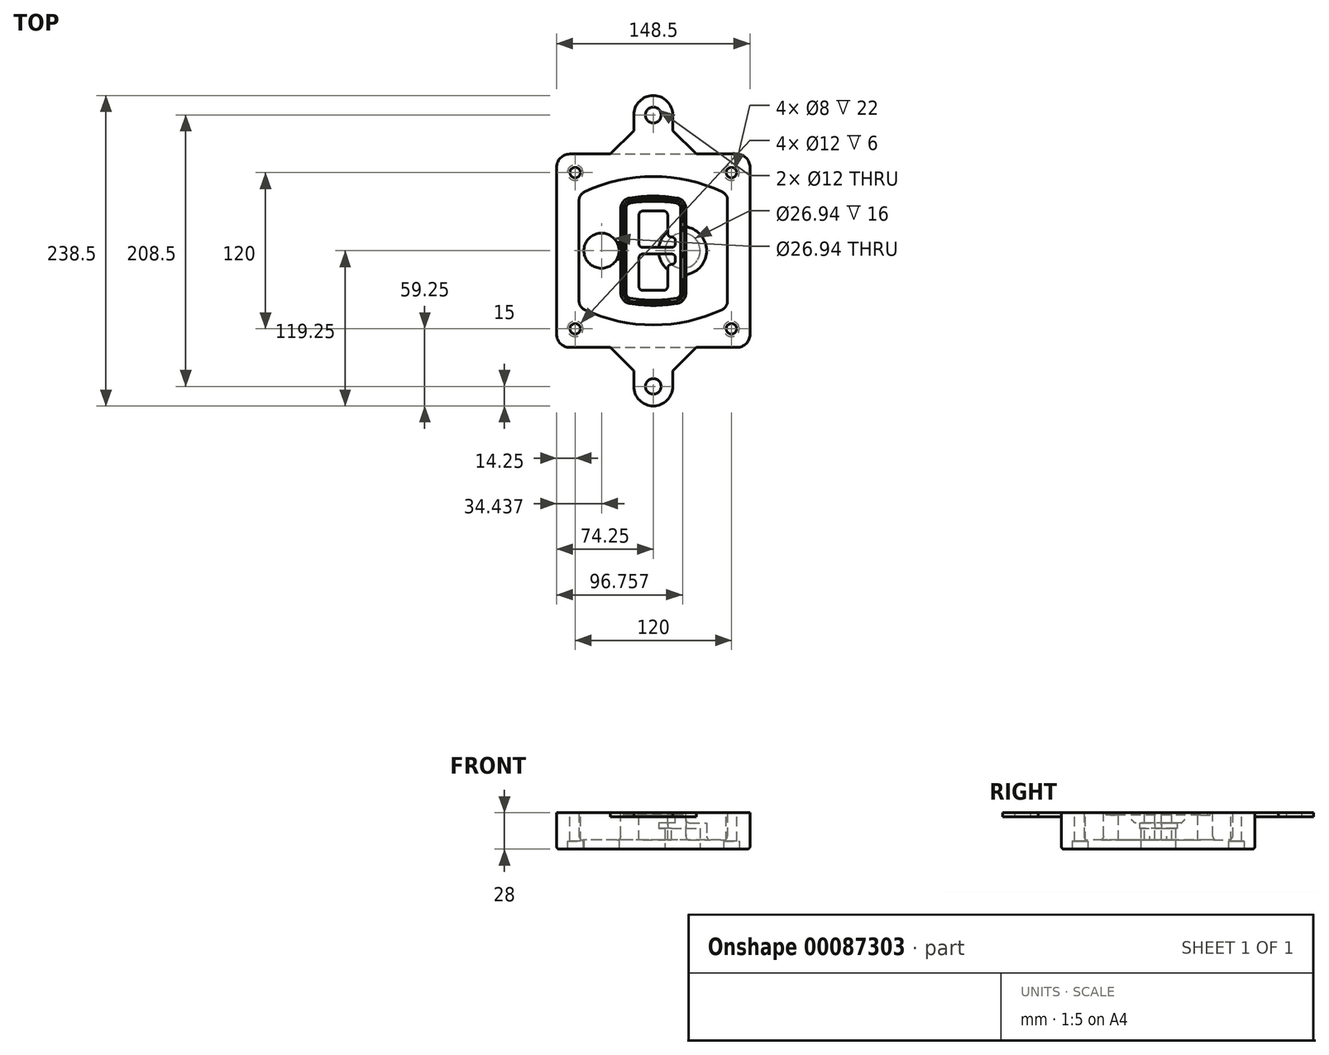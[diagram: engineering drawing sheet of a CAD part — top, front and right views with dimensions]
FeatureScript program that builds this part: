
annotation { "Feature Type Name" : "Feature", "Feature Type Description" : "" }
export const myFeature = defineFeature(function(context is Context, id is Id, definition is map)
    precondition{}
    {
        {
            var Q0;
            Q0=qCreatedBy(makeId("Top.planeOp"),FACE);
            var sketch = newSketch(context, id + "F0", { "sketchPlane" : qUnion([Q0])});
            skPoint(sketch, "E0.rect.middle", {"position": v(0, 0) * mm});
            skLineSegment(sketch, "E1.bottom", {"start": v(-64.25, -74.25) * mm, "end": v(64.25, -74.25) * mm});
            skLineSegment(sketch, "E1.top", {"start": v(-64.25, 74.25) * mm, "end": v(64.25, 74.25) * mm});
            skLineSegment(sketch, "E1.left", {"start": v(-74.25, -64.25) * mm, "end": v(-74.25, 64.25) * mm});
            skLineSegment(sketch, "E1.right", {"start": v(74.25, -64.25) * mm, "end": v(74.25, 64.25) * mm});
            skLineSegment(sketch, "E2", {"start": v(-74.25, 74.25) * mm, "end": v(74.25, -74.25) * mm, "construction": true});
            skLineSegment(sketch, "E3", {"start": v(74.25, 74.25) * mm, "end": v(-74.25, -74.25) * mm, "construction": true});
            skCircle(sketch, "E4", {"center": v(-60, 60) * mm, "radius": 4 * mm});
            skCircle(sketch, "E5", {"center": v(60, 60) * mm, "radius": 4 * mm});
            skCircle(sketch, "E6", {"center": v(60, -60) * mm, "radius": 4 * mm});
            skCircle(sketch, "E7", {"center": v(-60, -60) * mm, "radius": 4 * mm});
            skLineSegment(sketch, "E8", {"start": v(-60, 60) * mm, "end": v(60, 60) * mm, "construction": true});
            skLineSegment(sketch, "E9", {"start": v(60, 60) * mm, "end": v(60, -60) * mm, "construction": true});
            skLineSegment(sketch, "E10", {"start": v(60, -60) * mm, "end": v(-60, -60) * mm, "construction": true});
            skLineSegment(sketch, "E11", {"start": v(-60, -60) * mm, "end": v(-60, 60) * mm, "construction": true});
            skLineSegment(sketch, "E12", {"start": v(-60, 38.83) * mm, "end": v(-60, -38.83) * mm});
            skLineSegment(sketch, "E13", {"start": v(60, 38.83) * mm, "end": v(60, -38.83) * mm});
            skArc(sketch, "E14", {"start": v(54.26, 47.88) * mm, "mid": v(0, 60) * mm, "end": v(-54.26, 47.88) * mm});
            skArc(sketch, "E15", {"start": v(-54.26, -47.88) * mm, "mid": v(0, -60) * mm, "end": v(54.26, -47.88) * mm});
            skLineSegment(sketch, "E16", {"start": v(-60, 0) * mm, "end": v(60, 0) * mm, "construction": true});
            skPoint(sketch, "E17.visualSharp", {"position": v(-60, -45) * mm});
            skArc(sketch, "E17.filletArc", {"start": v(-60, -38.83) * mm, "mid": v(-58.44, -44.2) * mm, "end": v(-54.26, -47.88) * mm});
            skPoint(sketch, "E18.visualSharp", {"position": v(-60, 45) * mm});
            skArc(sketch, "E18.filletArc", {"start": v(-54.26, 47.88) * mm, "mid": v(-58.44, 44.2) * mm, "end": v(-60, 38.83) * mm});
            skPoint(sketch, "E19.visualSharp", {"position": v(60, 45) * mm});
            skArc(sketch, "E19.filletArc", {"start": v(60, 38.83) * mm, "mid": v(58.44, 44.2) * mm, "end": v(54.26, 47.88) * mm});
            skPoint(sketch, "E20.visualSharp", {"position": v(60, -45) * mm});
            skArc(sketch, "E20.filletArc", {"start": v(54.26, -47.88) * mm, "mid": v(58.44, -44.2) * mm, "end": v(60, -38.83) * mm});
            skPoint(sketch, "E21.visualSharp", {"position": v(-74.25, 74.25) * mm});
            skArc(sketch, "E21.filletArc", {"start": v(-64.25, 74.25) * mm, "mid": v(-71.32, 71.32) * mm, "end": v(-74.25, 64.25) * mm});
            skPoint(sketch, "E22.visualSharp", {"position": v(74.25, 74.25) * mm});
            skArc(sketch, "E22.filletArc", {"start": v(74.25, 64.25) * mm, "mid": v(71.32, 71.32) * mm, "end": v(64.25, 74.25) * mm});
            skPoint(sketch, "E23.visualSharp", {"position": v(74.25, -74.25) * mm});
            skArc(sketch, "E23.filletArc", {"start": v(64.25, -74.25) * mm, "mid": v(71.32, -71.32) * mm, "end": v(74.25, -64.25) * mm});
            skPoint(sketch, "E24.visualSharp", {"position": v(-74.25, -74.25) * mm});
            skArc(sketch, "E24.filletArc", {"start": v(-74.25, -64.25) * mm, "mid": v(-71.32, -71.32) * mm, "end": v(-64.25, -74.25) * mm});
            skArc(sketch, "E25.0", {"start": v(57, 38.83) * mm, "mid": v(55.9, 42.58) * mm, "end": v(52.98, 45.17) * mm});
            skLineSegment(sketch, "E25.1", {"start": v(57, 38.83) * mm, "end": v(57, -38.83) * mm});
            skArc(sketch, "E25.2", {"start": v(52.98, -45.17) * mm, "mid": v(55.9, -42.58) * mm, "end": v(57, -38.83) * mm});
            skArc(sketch, "E25.3", {"start": v(-52.98, -45.17) * mm, "mid": v(0, -57) * mm, "end": v(52.98, -45.17) * mm});
            skArc(sketch, "E25.4", {"start": v(-57, -38.83) * mm, "mid": v(-55.9, -42.58) * mm, "end": v(-52.98, -45.17) * mm});
            skArc(sketch, "E25.5", {"start": v(52.98, 45.17) * mm, "mid": v(0, 57) * mm, "end": v(-52.98, 45.17) * mm});
            skLineSegment(sketch, "E25.6", {"start": v(-57, 38.83) * mm, "end": v(-57, -38.83) * mm});
            skArc(sketch, "E25.7", {"start": v(-52.98, 45.17) * mm, "mid": v(-55.9, 42.58) * mm, "end": v(-57, 38.83) * mm});
            skArc(sketch, "E26.0", {"start": v(-55.96, 51.5) * mm, "mid": v(-61.82, 46.33) * mm, "end": v(-64, 38.83) * mm});
            skArc(sketch, "E26.1", {"start": v(55.96, 51.5) * mm, "mid": v(0, 64) * mm, "end": v(-55.96, 51.5) * mm});
            skArc(sketch, "E26.2", {"start": v(64, 38.83) * mm, "mid": v(61.82, 46.33) * mm, "end": v(55.96, 51.5) * mm});
            skLineSegment(sketch, "E26.3", {"start": v(64, 38.83) * mm, "end": v(64, -38.83) * mm});
            skArc(sketch, "E26.4", {"start": v(55.96, -51.5) * mm, "mid": v(61.82, -46.33) * mm, "end": v(64, -38.83) * mm});
            skLineSegment(sketch, "E26.5", {"start": v(-64, 38.83) * mm, "end": v(-64, -38.83) * mm});
            skArc(sketch, "E26.6", {"start": v(-55.96, -51.5) * mm, "mid": v(0, -64) * mm, "end": v(55.96, -51.5) * mm});
            skArc(sketch, "E26.7", {"start": v(-64, -38.83) * mm, "mid": v(-61.82, -46.33) * mm, "end": v(-55.96, -51.5) * mm});
            skSolve(sketch);
        }
        {
            var Q0;
            Q0=makeQuery(id+"F0.imprint","IMPRINT",FACE,{"disambiguationData":[TD([[makeQuery(id+"F0.imprint","IMPRINT",EDGE,{"derivedFrom":sQuery(id+"F0.wireOp",EDGE,"E1.bottom")}),1.0]])]});
            var Q1;
            Q1=makeQuery(id+"F0.imprint","IMPRINT",FACE,{"disambiguationData":[TD([[makeQuery(id+"F0.imprint","IMPRINT",EDGE,{"derivedFrom":sQuery(id+"F0.wireOp",EDGE,"E12")}),1.0]])]});
            var Q2;
            Q2=makeQuery(id+"F0.imprint","IMPRINT",FACE,{"disambiguationData":[TD([[makeQuery(id+"F0.imprint","IMPRINT",EDGE,{"derivedFrom":sQuery(id+"F0.wireOp",EDGE,"E25.0")}),1.0]])]});
            var Q3;
            Q3=makeQuery(id+"F0.imprint","IMPRINT",FACE,{"disambiguationData":[TD([[makeQuery(id+"F0.imprint","IMPRINT",EDGE,{"derivedFrom":sQuery(id+"F0.wireOp",EDGE,"E12")}),-1.0]])]});
            extrude(context, id + "F1", {"entities" : qUnion([Q0, Q1, Q2, Q3]), "oppositeDirection" : true, "depth" : 25 * mm});
        }
        {
            var Q0;
            Q0=makeQuery(id+"F0.imprint","IMPRINT",FACE,{"disambiguationData":[TD([[makeQuery(id+"F0.imprint","IMPRINT",EDGE,{"derivedFrom":sQuery(id+"F0.wireOp",EDGE,"E12")}),1.0]])]});
            extrude(context, id + "F2", {"entities" : qUnion([Q0]), "operationType" : NewBodyOperationType.ADD, "depth" : 3 * mm});
        }
        {
            var Q0;
            Q0=makeQuery(id+"F0.imprint","IMPRINT",FACE,{"disambiguationData":[TD([[makeQuery(id+"F0.imprint","IMPRINT",EDGE,{"derivedFrom":sQuery(id+"F0.wireOp",EDGE,"E25.0")}),1.0]])]});
            extrude(context, id + "F3", {"entities" : qUnion([Q0]), "operationType" : NewBodyOperationType.REMOVE, "oppositeDirection" : true, "depth" : 18 * mm});
        }
        {
            var Q0;
            Q0=makeQuery(id+"F2.opExtrude","CAP_FACE",FACE,{"disambiguationData":[OSD([sQuery(id+"F0.wireOp",EDGE,"E12"),sQuery(id+"F0.wireOp",EDGE,"E13"),sQuery(id+"F0.wireOp",EDGE,"E14"),sQuery(id+"F0.wireOp",EDGE,"E15"),sQuery(id+"F0.wireOp",EDGE,"E17.filletArc"),sQuery(id+"F0.wireOp",EDGE,"E18.filletArc"),sQuery(id+"F0.wireOp",EDGE,"E19.filletArc"),sQuery(id+"F0.wireOp",EDGE,"E20.filletArc"),sQuery(id+"F0.wireOp",EDGE,"E25.0"),sQuery(id+"F0.wireOp",EDGE,"E25.1"),sQuery(id+"F0.wireOp",EDGE,"E25.2"),sQuery(id+"F0.wireOp",EDGE,"E25.3"),sQuery(id+"F0.wireOp",EDGE,"E25.4"),sQuery(id+"F0.wireOp",EDGE,"E25.5"),sQuery(id+"F0.wireOp",EDGE,"E25.6"),sQuery(id+"F0.wireOp",EDGE,"E25.7")])],"isStart":false});
            var sketch = newSketch(context, id + "F4", { "sketchPlane" : qUnion([Q0])});
            skArc(sketch, "E27.0", {"start": v(-18.34, -40.45) * mm, "mid": v(0, -42) * mm, "end": v(18.34, -40.45) * mm});
            skArc(sketch, "E28.0", {"start": v(18.34, 40.45) * mm, "mid": v(0, 42) * mm, "end": v(-18.34, 40.45) * mm});
            skLineSegment(sketch, "E29", {"start": v(-25, 32.57) * mm, "end": v(-25, -32.57) * mm});
            skLineSegment(sketch, "E30", {"start": v(25, 32.57) * mm, "end": v(25, -32.57) * mm});
            skLineSegment(sketch, "E31", {"start": v(-25, 39.1) * mm, "end": v(25, 39.1) * mm, "construction": true});
            skLineSegment(sketch, "E32", {"start": v(-25, -39.1) * mm, "end": v(25, -39.1) * mm, "construction": true});
            skPoint(sketch, "E33.visualSharp", {"position": v(-25, 39.1) * mm});
            skArc(sketch, "E33.filletArc", {"start": v(-18.34, 40.45) * mm, "mid": v(-23.11, 37.73) * mm, "end": v(-25, 32.57) * mm});
            skPoint(sketch, "E34.visualSharp", {"position": v(25, 39.1) * mm});
            skArc(sketch, "E34.filletArc", {"start": v(25, 32.57) * mm, "mid": v(23.11, 37.73) * mm, "end": v(18.34, 40.45) * mm});
            skPoint(sketch, "E35.visualSharp", {"position": v(25, -39.1) * mm});
            skArc(sketch, "E35.filletArc", {"start": v(18.34, -40.45) * mm, "mid": v(23.11, -37.73) * mm, "end": v(25, -32.57) * mm});
            skPoint(sketch, "E36.visualSharp", {"position": v(-25, -39.1) * mm});
            skArc(sketch, "E36.filletArc", {"start": v(-25, -32.57) * mm, "mid": v(-23.11, -37.73) * mm, "end": v(-18.34, -40.45) * mm});
            skArc(sketch, "E37.0", {"start": v(52.98, 45.17) * mm, "mid": v(0, 57) * mm, "end": v(-52.98, 45.17) * mm});
            skArc(sketch, "E37.1", {"start": v(-52.98, 45.17) * mm, "mid": v(-55.9, 42.58) * mm, "end": v(-57, 38.83) * mm});
            skLineSegment(sketch, "E37.2", {"start": v(-57, 38.83) * mm, "end": v(-57, -38.83) * mm});
            skArc(sketch, "E37.3", {"start": v(-57, -38.83) * mm, "mid": v(-55.9, -42.58) * mm, "end": v(-52.98, -45.17) * mm});
            skArc(sketch, "E37.4", {"start": v(-52.98, -45.17) * mm, "mid": v(0, -57) * mm, "end": v(52.98, -45.17) * mm});
            skArc(sketch, "E37.5", {"start": v(52.98, -45.17) * mm, "mid": v(55.9, -42.58) * mm, "end": v(57, -38.83) * mm});
            skLineSegment(sketch, "E37.6", {"start": v(57, 38.83) * mm, "end": v(57, -38.83) * mm});
            skArc(sketch, "E37.7", {"start": v(57, 38.83) * mm, "mid": v(55.9, 42.58) * mm, "end": v(52.98, 45.17) * mm});
            skLineSegment(sketch, "E38.0", {"start": v(23, 32.57) * mm, "end": v(23, -32.57) * mm});
            skArc(sketch, "E38.1", {"start": v(18, -38.48) * mm, "mid": v(21.58, -36.44) * mm, "end": v(23, -32.57) * mm});
            skArc(sketch, "E38.2", {"start": v(-18, -38.48) * mm, "mid": v(0, -40) * mm, "end": v(18, -38.48) * mm});
            skArc(sketch, "E38.3", {"start": v(-23, -32.57) * mm, "mid": v(-21.58, -36.44) * mm, "end": v(-18, -38.48) * mm});
            skLineSegment(sketch, "E38.4", {"start": v(-23, 32.57) * mm, "end": v(-23, -32.57) * mm});
            skArc(sketch, "E38.5", {"start": v(23, 32.57) * mm, "mid": v(21.58, 36.44) * mm, "end": v(18, 38.48) * mm});
            skArc(sketch, "E38.6", {"start": v(-18, 38.48) * mm, "mid": v(-21.58, 36.44) * mm, "end": v(-23, 32.57) * mm});
            skArc(sketch, "E38.7", {"start": v(18, 38.48) * mm, "mid": v(0, 40) * mm, "end": v(-18, 38.48) * mm});
            skArc(sketch, "E39.0", {"start": v(21, 32.57) * mm, "mid": v(20.06, 35.15) * mm, "end": v(17.67, 36.5) * mm});
            skLineSegment(sketch, "E39.1", {"start": v(21, 32.57) * mm, "end": v(21, -32.57) * mm});
            skArc(sketch, "E39.2", {"start": v(17.67, -36.5) * mm, "mid": v(20.06, -35.15) * mm, "end": v(21, -32.57) * mm});
            skArc(sketch, "E39.3", {"start": v(-17.67, -36.5) * mm, "mid": v(0, -38) * mm, "end": v(17.67, -36.5) * mm});
            skArc(sketch, "E39.4", {"start": v(-21, -32.57) * mm, "mid": v(-20.06, -35.15) * mm, "end": v(-17.67, -36.5) * mm});
            skArc(sketch, "E39.5", {"start": v(17.67, 36.5) * mm, "mid": v(0, 38) * mm, "end": v(-17.67, 36.5) * mm});
            skLineSegment(sketch, "E39.6", {"start": v(-21, 32.57) * mm, "end": v(-21, -32.57) * mm});
            skArc(sketch, "E39.7", {"start": v(-17.67, 36.5) * mm, "mid": v(-20.06, 35.15) * mm, "end": v(-21, 32.57) * mm});
            skLineSegment(sketch, "E40", {"start": v(-25, 0) * mm, "end": v(25, 0) * mm, "construction": true});
            skLineSegment(sketch, "E41", {"start": v(-11, 5.5) * mm, "end": v(-11, 27.5) * mm});
            skLineSegment(sketch, "E42", {"start": v(-8, 30.5) * mm, "end": v(8, 30.5) * mm});
            skLineSegment(sketch, "E43", {"start": v(11, 27.5) * mm, "end": v(11, 13.5) * mm});
            skLineSegment(sketch, "E44", {"start": v(14, 10.5) * mm, "end": v(14, 10.5) * mm});
            skLineSegment(sketch, "E45", {"start": v(17, 7.5) * mm, "end": v(17, 5.5) * mm});
            skLineSegment(sketch, "E46", {"start": v(14, 2.5) * mm, "end": v(-8, 2.5) * mm});
            skPoint(sketch, "E47.visualSharp", {"position": v(-11, 30.5) * mm});
            skArc(sketch, "E47.filletArc", {"start": v(-8, 30.5) * mm, "mid": v(-10.12, 29.62) * mm, "end": v(-11, 27.5) * mm});
            skPoint(sketch, "E48.visualSharp", {"position": v(11, 30.5) * mm});
            skArc(sketch, "E48.filletArc", {"start": v(11, 27.5) * mm, "mid": v(10.12, 29.62) * mm, "end": v(8, 30.5) * mm});
            skPoint(sketch, "E49.visualSharp", {"position": v(11, 10.5) * mm});
            skArc(sketch, "E49.filletArc", {"start": v(11, 13.5) * mm, "mid": v(11.88, 11.38) * mm, "end": v(14, 10.5) * mm});
            skPoint(sketch, "E50.visualSharp", {"position": v(17, 10.5) * mm});
            skArc(sketch, "E50.filletArc", {"start": v(17, 7.5) * mm, "mid": v(16.12, 9.62) * mm, "end": v(14, 10.5) * mm});
            skPoint(sketch, "E51.visualSharp", {"position": v(17, 2.5) * mm});
            skArc(sketch, "E51.filletArc", {"start": v(14, 2.5) * mm, "mid": v(16.12, 3.38) * mm, "end": v(17, 5.5) * mm});
            skPoint(sketch, "E52.visualSharp", {"position": v(-11, 2.5) * mm});
            skArc(sketch, "E52.filletArc", {"start": v(-11, 5.5) * mm, "mid": v(-10.12, 3.38) * mm, "end": v(-8, 2.5) * mm});
            skLineSegment(sketch, "E53.0.MirrorCS", {"start": v(14, -2.5) * mm, "end": v(-8, -2.5) * mm});
            skArc(sketch, "E54.0.MirrorCS", {"start": v(-11, -5.5) * mm, "mid": v(-10.12, -3.38) * mm, "end": v(-8, -2.5) * mm});
            skLineSegment(sketch, "E55.0.MirrorCS", {"start": v(-11, -5.5) * mm, "end": v(-11, -27.5) * mm});
            skArc(sketch, "E56.0.MirrorCS", {"start": v(-8, -30.5) * mm, "mid": v(-10.12, -29.62) * mm, "end": v(-11, -27.5) * mm});
            skLineSegment(sketch, "E57.0.MirrorCS", {"start": v(-8, -30.5) * mm, "end": v(8, -30.5) * mm});
            skArc(sketch, "E58.0.MirrorCS", {"start": v(11, -27.5) * mm, "mid": v(10.12, -29.62) * mm, "end": v(8, -30.5) * mm});
            skLineSegment(sketch, "E59.0.MirrorCS", {"start": v(11, -27.5) * mm, "end": v(11, -13.5) * mm});
            skArc(sketch, "E60.0.MirrorCS", {"start": v(11, -13.5) * mm, "mid": v(11.88, -11.38) * mm, "end": v(14, -10.5) * mm});
            skArc(sketch, "E61.0.MirrorCS", {"start": v(17, -7.5) * mm, "mid": v(16.12, -9.62) * mm, "end": v(14, -10.5) * mm});
            skLineSegment(sketch, "E62.0.MirrorCS", {"start": v(17, -7.5) * mm, "end": v(17, -5.5) * mm});
            skArc(sketch, "E63.0.MirrorCS", {"start": v(14, -2.5) * mm, "mid": v(16.12, -3.38) * mm, "end": v(17, -5.5) * mm});
            skSolve(sketch);
        }
        {
            var Q0;
            Q0=makeQuery(id+"F4.imprint","IMPRINT",FACE,{"disambiguationData":[TD([[makeQuery(id+"F4.imprint","IMPRINT",EDGE,{"derivedFrom":sQuery(id+"F4.wireOp",EDGE,"E27.0")}),1.0]])]});
            var Q1;
            Q1=makeQuery(id+"F4.imprint","IMPRINT",FACE,{"disambiguationData":[TD([[makeQuery(id+"F4.imprint","IMPRINT",EDGE,{"derivedFrom":sQuery(id+"F4.wireOp",EDGE,"E38.0")}),-1.0]])]});
            var Q2;
            Q2=makeQuery(id+"F4.imprint","IMPRINT",FACE,{"disambiguationData":[TD([[makeQuery(id+"F4.imprint","IMPRINT",EDGE,{"derivedFrom":sQuery(id+"F4.wireOp",EDGE,"E39.0")}),1.0]])]});
            extrude(context, id + "F5", {"entities" : qUnion([Q0, Q1, Q2]), "operationType" : NewBodyOperationType.ADD, "endBound" : BoundingType.UP_TO_NEXT, "oppositeDirection" : true, "depth" : 25 * mm});
        }
        {
            var Q0;
            Q0=makeQuery(id+"F4.imprint","IMPRINT",FACE,{"disambiguationData":[TD([[makeQuery(id+"F4.imprint","IMPRINT",EDGE,{"derivedFrom":sQuery(id+"F4.wireOp",EDGE,"E38.0")}),-1.0]])]});
            extrude(context, id + "F6", {"entities" : qUnion([Q0]), "operationType" : NewBodyOperationType.REMOVE, "oppositeDirection" : true, "depth" : 2 * mm});
        }
        {
            var Q0;
            Q0=makeQuery(id+"F1.opExtrude","CAP_FACE",FACE,{"disambiguationData":[OSD([sQuery(id+"F0.wireOp",EDGE,"E1.bottom"),sQuery(id+"F0.wireOp",EDGE,"E1.top"),sQuery(id+"F0.wireOp",EDGE,"E1.left"),sQuery(id+"F0.wireOp",EDGE,"E1.right"),sQuery(id+"F0.wireOp",EDGE,"E4"),sQuery(id+"F0.wireOp",EDGE,"E5"),sQuery(id+"F0.wireOp",EDGE,"E6"),sQuery(id+"F0.wireOp",EDGE,"E7"),sQuery(id+"F0.wireOp",EDGE,"E21.filletArc"),sQuery(id+"F0.wireOp",EDGE,"E22.filletArc"),sQuery(id+"F0.wireOp",EDGE,"E23.filletArc"),sQuery(id+"F0.wireOp",EDGE,"E24.filletArc")])],"isStart":false});
            var sketch = newSketch(context, id + "F7", { "sketchPlane" : qUnion([Q0])});
            skCircle(sketch, "E64", {"center": v(22.5, 0) * mm, "radius": 13.47 * mm});
            skCircle(sketch, "E65", {"center": v(-39.81, 0) * mm, "radius": 13.47 * mm});
            skLineSegment(sketch, "E66", {"start": v(74.25, 0) * mm, "end": v(-74.25, 0) * mm});
            skCircle(sketch, "E67", {"center": v(22.5, 0) * mm, "radius": 18.47 * mm});
            skCircle(sketch, "E68", {"center": v(60, -60) * mm, "radius": 6 * mm});
            skCircle(sketch, "E69", {"center": v(-60, -60) * mm, "radius": 6 * mm});
            skCircle(sketch, "E70", {"center": v(-60, 60) * mm, "radius": 6 * mm});
            skCircle(sketch, "E71", {"center": v(60, 60) * mm, "radius": 6 * mm});
            skSolve(sketch);
        }
        {
            var Q0;
            {var subQ1=sQuery(id+"F7.wireOp",EDGE,"E66");var subQ4=sQuery(id+"F7.wireOp",EDGE,"E64");var subQ6=makeQuery(id+"F7.imprint","INTERSECT",VERTEX,{"disambiguationData":[OD(0.0)],"derivedFrom":[subQ4,subQ1]});Q0=makeQuery(id+"F7.imprint","IMPRINT",FACE,{"disambiguationData":[TD([[makeQuery(id+"F7.imprint","IMPRINT",EDGE,{"disambiguationData":[TD([[subQ6,-1.0]])],"derivedFrom":subQ4}),-1.0]])]});}
            var Q1;
            {var subQ0=sQuery(id+"F7.wireOp",EDGE,"E66");var subQ1=sQuery(id+"F7.wireOp",EDGE,"E64");var subQ3=makeQuery(id+"F7.imprint","INTERSECT",VERTEX,{"disambiguationData":[OD(0.0)],"derivedFrom":[subQ1,subQ0]});Q1=makeQuery(id+"F7.imprint","IMPRINT",FACE,{"disambiguationData":[TD([[makeQuery(id+"F7.imprint","IMPRINT",EDGE,{"disambiguationData":[TD([[subQ3,-1.0]])],"derivedFrom":subQ1}),1.0]])]});}
            var Q2;
            {var subQ0=sQuery(id+"F7.wireOp",EDGE,"E66");var subQ1=sQuery(id+"F7.wireOp",EDGE,"E64");var subQ3=makeQuery(id+"F7.imprint","INTERSECT",VERTEX,{"disambiguationData":[OD(0.0)],"derivedFrom":[subQ1,subQ0]});Q2=makeQuery(id+"F7.imprint","IMPRINT",FACE,{"disambiguationData":[TD([[makeQuery(id+"F7.imprint","IMPRINT",EDGE,{"disambiguationData":[TD([[subQ3,1.0]])],"derivedFrom":subQ1}),1.0]])]});}
            var Q3;
            {var subQ1=sQuery(id+"F7.wireOp",EDGE,"E66");var subQ4=sQuery(id+"F7.wireOp",EDGE,"E64");var subQ6=makeQuery(id+"F7.imprint","INTERSECT",VERTEX,{"disambiguationData":[OD(0.0)],"derivedFrom":[subQ4,subQ1]});Q3=makeQuery(id+"F7.imprint","IMPRINT",FACE,{"disambiguationData":[TD([[makeQuery(id+"F7.imprint","IMPRINT",EDGE,{"disambiguationData":[TD([[subQ6,1.0]])],"derivedFrom":subQ4}),-1.0]])]});}
            extrude(context, id + "F8", {"entities" : qUnion([Q0, Q1, Q2, Q3]), "operationType" : NewBodyOperationType.ADD, "oppositeDirection" : true, "depth" : 20 * mm});
        }
        {
            var Q0;
            {var subQ0=sQuery(id+"F7.wireOp",EDGE,"E66");var subQ1=sQuery(id+"F7.wireOp",EDGE,"E64");var subQ3=makeQuery(id+"F7.imprint","INTERSECT",VERTEX,{"disambiguationData":[OD(0.0)],"derivedFrom":[subQ1,subQ0]});Q0=makeQuery(id+"F7.imprint","IMPRINT",FACE,{"disambiguationData":[TD([[makeQuery(id+"F7.imprint","IMPRINT",EDGE,{"disambiguationData":[TD([[subQ3,-1.0]])],"derivedFrom":subQ1}),1.0]])]});}
            var Q1;
            {var subQ0=sQuery(id+"F7.wireOp",EDGE,"E66");var subQ1=sQuery(id+"F7.wireOp",EDGE,"E64");var subQ3=makeQuery(id+"F7.imprint","INTERSECT",VERTEX,{"disambiguationData":[OD(0.0)],"derivedFrom":[subQ1,subQ0]});Q1=makeQuery(id+"F7.imprint","IMPRINT",FACE,{"disambiguationData":[TD([[makeQuery(id+"F7.imprint","IMPRINT",EDGE,{"disambiguationData":[TD([[subQ3,1.0]])],"derivedFrom":subQ1}),1.0]])]});}
            extrude(context, id + "F9", {"entities" : qUnion([Q0, Q1]), "operationType" : NewBodyOperationType.REMOVE, "oppositeDirection" : true, "depth" : 16 * mm});
        }
        {
            var Q0;
            {var subQ0=sQuery(id+"F7.wireOp",EDGE,"E66");var subQ1=sQuery(id+"F7.wireOp",EDGE,"E65");var subQ3=makeQuery(id+"F7.imprint","INTERSECT",VERTEX,{"disambiguationData":[OD(0.0)],"derivedFrom":[subQ1,subQ0]});Q0=makeQuery(id+"F7.imprint","IMPRINT",FACE,{"disambiguationData":[TD([[makeQuery(id+"F7.imprint","IMPRINT",EDGE,{"disambiguationData":[TD([[subQ3,-1.0]])],"derivedFrom":subQ1}),1.0]])]});}
            var Q1;
            {var subQ0=sQuery(id+"F7.wireOp",EDGE,"E66");var subQ1=sQuery(id+"F7.wireOp",EDGE,"E65");var subQ3=makeQuery(id+"F7.imprint","INTERSECT",VERTEX,{"disambiguationData":[OD(0.0)],"derivedFrom":[subQ1,subQ0]});Q1=makeQuery(id+"F7.imprint","IMPRINT",FACE,{"disambiguationData":[TD([[makeQuery(id+"F7.imprint","IMPRINT",EDGE,{"disambiguationData":[TD([[subQ3,1.0]])],"derivedFrom":subQ1}),1.0]])]});}
            extrude(context, id + "F10", {"entities" : qUnion([Q0, Q1]), "operationType" : NewBodyOperationType.REMOVE, "oppositeDirection" : true, "depth" : 25 * mm});
        }
        {
            var Q0;
            Q0=makeQuery(id+"F7.imprint","IMPRINT",FACE,{"disambiguationData":[TD([[makeQuery(id+"F7.imprint","IMPRINT",EDGE,{"derivedFrom":sQuery(id+"F7.wireOp",EDGE,"E68")}),1.0]])]});
            var Q1;
            Q1=makeQuery(id+"F7.imprint","IMPRINT",FACE,{"disambiguationData":[TD([[makeQuery(id+"F7.imprint","IMPRINT",EDGE,{"derivedFrom":makeQuery(id+"F1.opExtrude","CAP_EDGE",EDGE,{"disambiguationData":[OSD([sQuery(id+"F0.wireOp",EDGE,"E5")])],"isStart":false})}),-1.0]])]});
            var Q2;
            Q2=makeQuery(id+"F7.imprint","IMPRINT",FACE,{"disambiguationData":[TD([[makeQuery(id+"F7.imprint","IMPRINT",EDGE,{"derivedFrom":sQuery(id+"F7.wireOp",EDGE,"E69")}),1.0]])]});
            var Q3;
            Q3=makeQuery(id+"F7.imprint","IMPRINT",FACE,{"disambiguationData":[TD([[makeQuery(id+"F7.imprint","IMPRINT",EDGE,{"derivedFrom":makeQuery(id+"F1.opExtrude","CAP_EDGE",EDGE,{"disambiguationData":[OSD([sQuery(id+"F0.wireOp",EDGE,"E4")])],"isStart":false})}),-1.0]])]});
            var Q4;
            Q4=makeQuery(id+"F7.imprint","IMPRINT",FACE,{"disambiguationData":[TD([[makeQuery(id+"F7.imprint","IMPRINT",EDGE,{"derivedFrom":sQuery(id+"F7.wireOp",EDGE,"E70")}),1.0]])]});
            var Q5;
            Q5=makeQuery(id+"F7.imprint","IMPRINT",FACE,{"disambiguationData":[TD([[makeQuery(id+"F7.imprint","IMPRINT",EDGE,{"derivedFrom":makeQuery(id+"F1.opExtrude","CAP_EDGE",EDGE,{"disambiguationData":[OSD([sQuery(id+"F0.wireOp",EDGE,"E7")])],"isStart":false})}),-1.0]])]});
            var Q6;
            Q6=makeQuery(id+"F7.imprint","IMPRINT",FACE,{"disambiguationData":[TD([[makeQuery(id+"F7.imprint","IMPRINT",EDGE,{"derivedFrom":sQuery(id+"F7.wireOp",EDGE,"E71")}),1.0]])]});
            var Q7;
            Q7=makeQuery(id+"F7.imprint","IMPRINT",FACE,{"disambiguationData":[TD([[makeQuery(id+"F7.imprint","IMPRINT",EDGE,{"derivedFrom":makeQuery(id+"F1.opExtrude","CAP_EDGE",EDGE,{"disambiguationData":[OSD([sQuery(id+"F0.wireOp",EDGE,"E6")])],"isStart":false})}),-1.0]])]});
            extrude(context, id + "F11", {"entities" : qUnion([Q0, Q1, Q2, Q3, Q4, Q5, Q6, Q7]), "operationType" : NewBodyOperationType.REMOVE, "oppositeDirection" : true, "depth" : 6 * mm});
        }
        {
            var Q0;
            Q0=makeQuery(id+"F9.boolean.opBoolean","COPY",FACE,{"derivedFrom":makeQuery(id+"F9.opExtrude","CAP_FACE",FACE,{"disambiguationData":[OSD([sQuery(id+"F7.wireOp",EDGE,"E64")])],"isStart":false})});
            var sketch = newSketch(context, id + "F12", { "sketchPlane" : qUnion([Q0])});
            skArc(sketch, "E72.0", {"start": v(11, 14.45) * mm, "mid": v(6.45, 9.13) * mm, "end": v(4.2, 2.5) * mm});
            skArc(sketch, "E72.1", {"start": v(4.2, -2.5) * mm, "mid": v(6.45, -9.13) * mm, "end": v(11, -14.45) * mm});
            skLineSegment(sketch, "E73", {"start": v(4.2, -2.5) * mm, "end": v(14, -2.5) * mm});
            skLineSegment(sketch, "E74.0", {"start": v(14, 2.5) * mm, "end": v(4.2, 2.5) * mm});
            skArc(sketch, "E74.1", {"start": v(14, 2.5) * mm, "mid": v(16.12, 3.38) * mm, "end": v(17, 5.5) * mm});
            skLineSegment(sketch, "E74.2", {"start": v(17, 7.5) * mm, "end": v(17, 5.5) * mm});
            skArc(sketch, "E74.3", {"start": v(17, 7.5) * mm, "mid": v(16.12, 9.62) * mm, "end": v(14, 10.5) * mm});
            skArc(sketch, "E74.4", {"start": v(11, 13.5) * mm, "mid": v(11.88, 11.38) * mm, "end": v(14, 10.5) * mm});
            skLineSegment(sketch, "E74.5", {"start": v(11, 14.45) * mm, "end": v(11, 13.5) * mm});
            skLineSegment(sketch, "E74.7", {"start": v(14, -2.5) * mm, "end": v(4.2, -2.5) * mm});
            skArc(sketch, "E74.8", {"start": v(14, -2.5) * mm, "mid": v(16.12, -3.38) * mm, "end": v(17, -5.5) * mm});
            skLineSegment(sketch, "E74.9", {"start": v(17, -7.5) * mm, "end": v(17, -5.5) * mm});
            skArc(sketch, "E74.10", {"start": v(17, -7.5) * mm, "mid": v(16.12, -9.62) * mm, "end": v(14, -10.5) * mm});
            skArc(sketch, "E74.11", {"start": v(11, -13.5) * mm, "mid": v(11.88, -11.38) * mm, "end": v(14, -10.5) * mm});
            skLineSegment(sketch, "E74.12", {"start": v(11, -14.45) * mm, "end": v(11, -13.5) * mm});
            skPoint(sketch, "E75.orphan", {"position": v(11, -27.5) * mm});
            skPoint(sketch, "E76.orphan", {"position": v(-8, -2.5) * mm});
            skPoint(sketch, "E77.orphan", {"position": v(-8, 2.5) * mm});
            skPoint(sketch, "E78.orphan", {"position": v(11, 27.5) * mm});
            skSolve(sketch);
        }
        {
            var Q0;
            {var subQ7=sQuery(id+"F12.wireOp",EDGE,"E72.0");var subQ14=sQuery(id+"F12.wireOp",EDGE,"E72.1");var subQ16=sQuery(id+"F12.wireOp",EDGE,"E74.1");var subQ18=sQuery(id+"F12.wireOp",EDGE,"E74.8");Q0=qUnion([makeQuery(id+"F12.imprint","IMPRINT",FACE,{"disambiguationData":[TD([[makeQuery(id+"F12.imprint","IMPRINT",EDGE,{"derivedFrom":subQ7}),1.0]])]}),makeQuery(id+"F12.imprint","IMPRINT",FACE,{"disambiguationData":[TD([[makeQuery(id+"F12.imprint","IMPRINT",EDGE,{"derivedFrom":subQ14}),1.0]])]}),makeQuery(id+"F12.imprint","IMPRINT",FACE,{"disambiguationData":[TD([[makeQuery(id+"F12.imprint","IMPRINT",EDGE,{"derivedFrom":subQ16}),1.0]])]}),makeQuery(id+"F12.imprint","IMPRINT",FACE,{"disambiguationData":[TD([[makeQuery(id+"F12.imprint","IMPRINT",EDGE,{"derivedFrom":subQ18}),-1.0]])]})]);}
            var Q1;
            Q1=makeQuery(id+"F5.boolean.opBoolean","SPLIT",FACE,{"disambiguationData":[TD([makeQuery(id+"F5.opExtrude","SWEPT_FACE",FACE,{"disambiguationData":[OSD([sQuery(id+"F4.wireOp",EDGE,"E41")])]})])],"derivedFrom":makeQuery(id+"F3.boolean.opBoolean","COPY",FACE,{"derivedFrom":makeQuery(id+"F3.opExtrude","CAP_FACE",FACE,{"disambiguationData":[OSD([sQuery(id+"F0.wireOp",EDGE,"E25.0"),sQuery(id+"F0.wireOp",EDGE,"E25.1"),sQuery(id+"F0.wireOp",EDGE,"E25.2"),sQuery(id+"F0.wireOp",EDGE,"E25.3"),sQuery(id+"F0.wireOp",EDGE,"E25.4"),sQuery(id+"F0.wireOp",EDGE,"E25.5"),sQuery(id+"F0.wireOp",EDGE,"E25.6"),sQuery(id+"F0.wireOp",EDGE,"E25.7")])],"isStart":false})})});
            extrude(context, id + "F13", {"entities" : qUnion([Q0]), "operationType" : NewBodyOperationType.REMOVE, "endBound" : BoundingType.UP_TO_SURFACE, "endBoundEntityFace" : qUnion([Q1]), "depth" : 25 * mm});
        }
        {
            var Q0;
            Q0=makeQuery(id+"F3.boolean.opBoolean","COPY",EDGE,{"derivedFrom":makeQuery(id+"F3.opExtrude","CAP_EDGE",EDGE,{"disambiguationData":[OSD([sQuery(id+"F0.wireOp",EDGE,"E25.6")])],"isStart":false})});
            var Q1;
            Q1=makeQuery(id+"F8.boolean.opBoolean","INTERSECT",EDGE,{"derivedFrom":[makeQuery(id+"F5.opExtrude","SWEPT_FACE",FACE,{"disambiguationData":[OSD([sQuery(id+"F4.wireOp",EDGE,"E30")])]}),makeQuery(id+"F8.opExtrude","CAP_FACE",FACE,{"disambiguationData":[OSD([sQuery(id+"F7.wireOp",EDGE,"E67")])],"isStart":false})]});
            var Q2;
            Q2=makeQuery(id+"F8.boolean.opBoolean","INTERSECT",EDGE,{"disambiguationData":[OD(1.0)],"derivedFrom":[makeQuery(id+"F5.opExtrude","SWEPT_FACE",FACE,{"disambiguationData":[OSD([sQuery(id+"F4.wireOp",EDGE,"E30")])]}),makeQuery(id+"F8.opExtrude","SWEPT_FACE",FACE,{"disambiguationData":[OSD([sQuery(id+"F7.wireOp",EDGE,"E67")])]})]});
            var Q3;
            {var subQ0=sQuery(id+"F4.wireOp",EDGE,"E30");Q3=makeQuery(id+"F8.boolean.opBoolean","SPLIT",EDGE,{"disambiguationData":[TD([makeQuery(id+"F5.opExtrude","SWEPT_FACE",FACE,{"disambiguationData":[OSD([sQuery(id+"F4.wireOp",EDGE,"E35.filletArc")])]})])],"derivedFrom":makeQuery(id+"F5.opExtrude","CAP_EDGE",EDGE,{"disambiguationData":[OSD([subQ0])],"isStart":false})});}
            var Q4;
            {var subQ0=sQuery(id+"F0.wireOp",EDGE,"E25.7");var subQ1=sQuery(id+"F0.wireOp",EDGE,"E25.1");var subQ2=sQuery(id+"F0.wireOp",EDGE,"E25.6");var subQ3=sQuery(id+"F0.wireOp",EDGE,"E25.5");var subQ4=sQuery(id+"F0.wireOp",EDGE,"E25.4");var subQ5=sQuery(id+"F0.wireOp",EDGE,"E25.0");var subQ6=sQuery(id+"F0.wireOp",EDGE,"E25.2");var subQ7=sQuery(id+"F0.wireOp",EDGE,"E25.3");Q4=makeQuery(id+"F8.boolean.opBoolean","INTERSECT",EDGE,{"derivedFrom":[makeQuery(id+"F5.boolean.opBoolean","SPLIT",FACE,{"disambiguationData":[TD([makeQuery(id+"F2.opExtrude","SWEPT_FACE",FACE,{"disambiguationData":[OSD([subQ5])]})])],"derivedFrom":makeQuery(id+"F3.boolean.opBoolean","COPY",FACE,{"derivedFrom":makeQuery(id+"F3.opExtrude","CAP_FACE",FACE,{"disambiguationData":[OSD([subQ5,subQ1,subQ6,subQ7,subQ4,subQ3,subQ2,subQ0])],"isStart":false})})}),makeQuery(id+"F8.opExtrude","SWEPT_FACE",FACE,{"disambiguationData":[OSD([sQuery(id+"F7.wireOp",EDGE,"E67")])]})]});}
            var Q5;
            Q5=makeQuery(id+"F8.boolean.opBoolean","INTERSECT",EDGE,{"disambiguationData":[OD(0.0)],"derivedFrom":[makeQuery(id+"F5.opExtrude","SWEPT_FACE",FACE,{"disambiguationData":[OSD([sQuery(id+"F4.wireOp",EDGE,"E30")])]}),makeQuery(id+"F8.opExtrude","SWEPT_FACE",FACE,{"disambiguationData":[OSD([sQuery(id+"F7.wireOp",EDGE,"E67")])]})]});
            fillet(context, id + "F14", {"entities" : qUnion([Q0, Q1, Q2, Q3, Q4, Q5]), "radius" : 3 * mm, "tangentPropagation" : true, "allowEdgeOverflow" : false});
        }
        {
            var Q0;
            Q0=makeQuery(id+"F1.opExtrude","CAP_EDGE",EDGE,{"disambiguationData":[OSD([sQuery(id+"F0.wireOp",EDGE,"E1.bottom")])],"isStart":false});
            fillet(context, id + "F15", {"entities" : qUnion([Q0]), "radius" : 2 * mm, "tangentPropagation" : true, "allowEdgeOverflow" : false});
        }
        {
            var Q0;
            Q0=qCreatedBy(makeId("Top.planeOp"),FACE);
            var sketch = newSketch(context, id + "F16", { "sketchPlane" : qUnion([Q0])});
            skLineSegment(sketch, "E79.0", {"start": v(-64.25, 74.25) * mm, "end": v(64.25, 74.25) * mm});
            skLineSegment(sketch, "E80.0", {"start": v(-64.25, -74.25) * mm, "end": v(64.25, -74.25) * mm});
            skLineSegment(sketch, "E81", {"start": v(0, 74.25) * mm, "end": v(0, 104.25) * mm, "construction": true});
            skCircle(sketch, "E82", {"center": v(0, 104.25) * mm, "radius": 6 * mm});
            skLineSegment(sketch, "E83", {"start": v(15, 104.25) * mm, "end": v(15, 92.25) * mm});
            skLineSegment(sketch, "E84", {"start": v(-15, 104.25) * mm, "end": v(-15, 92.25) * mm});
            skLineSegment(sketch, "E85", {"start": v(-15, 92.25) * mm, "end": v(-33, 74.25) * mm});
            skLineSegment(sketch, "E86", {"start": v(15, 92.25) * mm, "end": v(33, 74.25) * mm});
            skArc(sketch, "E87", {"start": v(15, 104.25) * mm, "mid": v(0, 119.25) * mm, "end": v(-15, 104.25) * mm});
            skLineSegment(sketch, "E88", {"start": v(0, 0) * mm, "end": v(107.6, 0) * mm, "construction": true});
            skLineSegment(sketch, "E89.MirrorCS", {"start": v(-15, 122.25) * mm, "end": v(-33, 140.25) * mm});
            skLineSegment(sketch, "E90.MirrorCS", {"start": v(-33, 107.25) * mm, "end": v(-3, 107.25) * mm, "construction": true});
            skArc(sketch, "E91.MirrorCS", {"start": v(-15, 104.25) * mm, "mid": v(0, 119.25) * mm, "end": v(15, 104.25) * mm});
            skLineSegment(sketch, "E92.MirrorCS", {"start": v(64.25, 74.25) * mm, "end": v(-64.25, 74.25) * mm});
            skLineSegment(sketch, "E93.MirrorCS", {"start": v(15, -92.25) * mm, "end": v(33, -74.25) * mm});
            skLineSegment(sketch, "E94.MirrorCS", {"start": v(15, -104.25) * mm, "end": v(15, -92.25) * mm});
            skCircle(sketch, "E95.MirrorC", {"center": v(0, -104.25) * mm, "radius": 6 * mm});
            skArc(sketch, "E96.MirrorCS", {"start": v(15, -104.25) * mm, "mid": v(0, -119.25) * mm, "end": v(-15, -104.25) * mm});
            skLineSegment(sketch, "E97.MirrorCS", {"start": v(-15, -104.25) * mm, "end": v(-15, -92.25) * mm});
            skLineSegment(sketch, "E98.MirrorCS", {"start": v(-15, -92.25) * mm, "end": v(-33, -74.25) * mm});
            skSolve(sketch);
        }
        {
            var Q0;
            {var subQ0=sQuery(id+"F16.wireOp",EDGE,"E85");Q0=makeQuery(id+"F16.imprint","IMPRINT",FACE,{"disambiguationData":[TD([[makeQuery(id+"F16.imprint","IMPRINT",EDGE,{"derivedFrom":subQ0}),1.0]])]});}
            var Q1;
            {var subQ0=sQuery(id+"F0.wireOp",EDGE,"E22.filletArc");var subQ1=sQuery(id+"F0.wireOp",EDGE,"E7");var subQ2=sQuery(id+"F0.wireOp",EDGE,"E6");var subQ3=sQuery(id+"F0.wireOp",EDGE,"E5");var subQ4=sQuery(id+"F0.wireOp",EDGE,"E4");var subQ5=sQuery(id+"F0.wireOp",EDGE,"E1.bottom");var subQ6=sQuery(id+"F0.wireOp",EDGE,"E21.filletArc");var subQ7=sQuery(id+"F0.wireOp",EDGE,"E1.top");var subQ8=sQuery(id+"F0.wireOp",EDGE,"E1.left");var subQ9=sQuery(id+"F0.wireOp",EDGE,"E1.right");var subQ10=sQuery(id+"F0.wireOp",EDGE,"E23.filletArc");var subQ11=sQuery(id+"F0.wireOp",EDGE,"E24.filletArc");Q1=makeQuery(id+"F2.boolean.opBoolean","SPLIT",FACE,{"disambiguationData":[TD([makeQuery(id+"F1.opExtrude","SWEPT_FACE",FACE,{"disambiguationData":[OSD([subQ5])]})])],"derivedFrom":makeQuery(id+"F1.opExtrude","CAP_FACE",FACE,{"disambiguationData":[OSD([subQ5,subQ7,subQ8,subQ9,subQ4,subQ3,subQ2,subQ1,subQ6,subQ0,subQ10,subQ11])],"isStart":true})});}
            var Q2;
            {var subQ1=sQuery(id+"F16.wireOp",EDGE,"E93.MirrorCS");Q2=makeQuery(id+"F16.imprint","IMPRINT",FACE,{"disambiguationData":[TD([[makeQuery(id+"F16.imprint","IMPRINT",EDGE,{"derivedFrom":subQ1}),1.0]])]});}
            var Q3;
            Q3=makeQuery(id+"F2.opExtrude","CAP_FACE",FACE,{"disambiguationData":[OSD([sQuery(id+"F0.wireOp",EDGE,"E12"),sQuery(id+"F0.wireOp",EDGE,"E13"),sQuery(id+"F0.wireOp",EDGE,"E14"),sQuery(id+"F0.wireOp",EDGE,"E15"),sQuery(id+"F0.wireOp",EDGE,"E17.filletArc"),sQuery(id+"F0.wireOp",EDGE,"E18.filletArc"),sQuery(id+"F0.wireOp",EDGE,"E19.filletArc"),sQuery(id+"F0.wireOp",EDGE,"E20.filletArc"),sQuery(id+"F0.wireOp",EDGE,"E25.0"),sQuery(id+"F0.wireOp",EDGE,"E25.1"),sQuery(id+"F0.wireOp",EDGE,"E25.2"),sQuery(id+"F0.wireOp",EDGE,"E25.3"),sQuery(id+"F0.wireOp",EDGE,"E25.4"),sQuery(id+"F0.wireOp",EDGE,"E25.5"),sQuery(id+"F0.wireOp",EDGE,"E25.6"),sQuery(id+"F0.wireOp",EDGE,"E25.7")])],"isStart":false});
            extrude(context, id + "F17", {"entities" : qUnion([Q0, Q1, Q2]), "operationType" : NewBodyOperationType.ADD, "endBound" : BoundingType.UP_TO_SURFACE, "endBoundEntityFace" : qUnion([Q3]), "depth" : 25 * mm});
        }
    });
